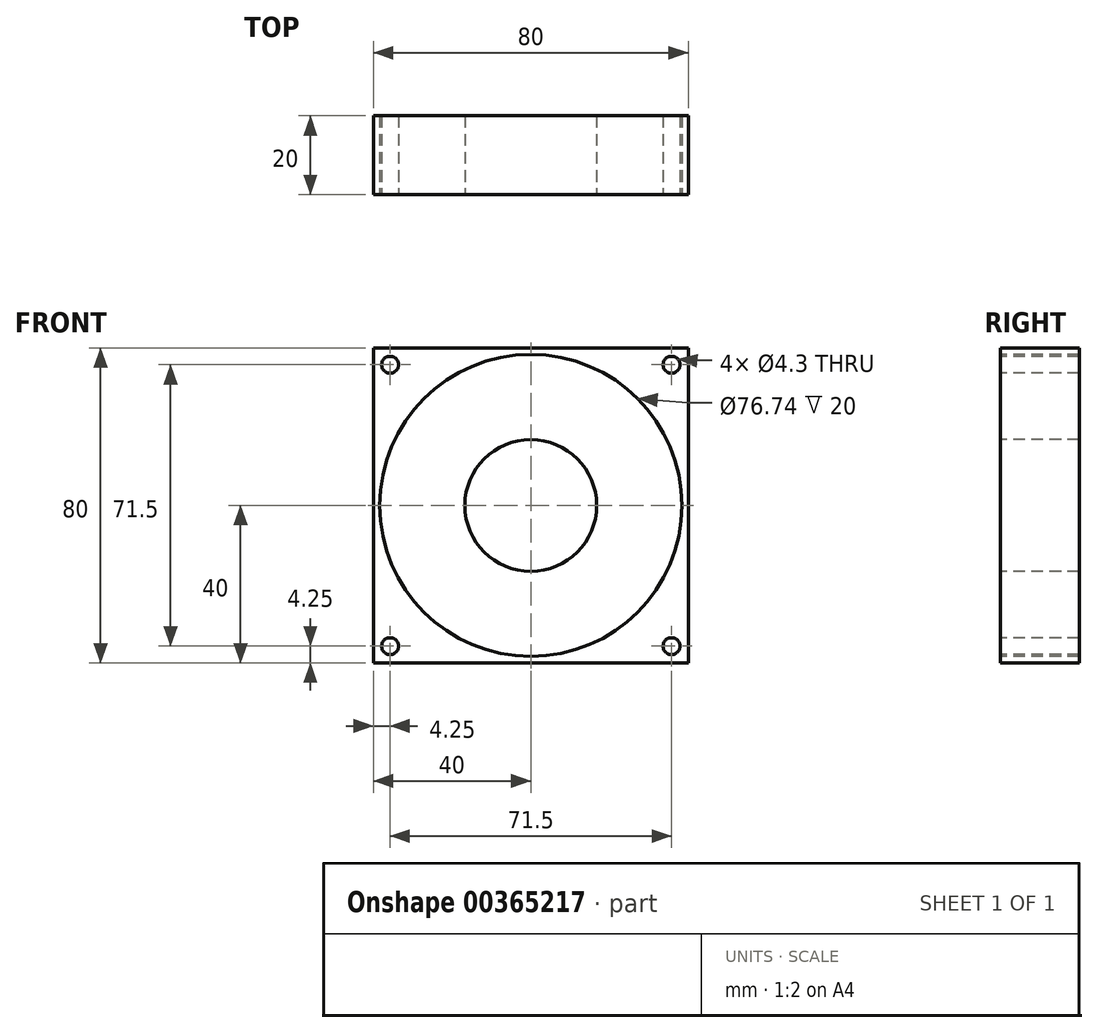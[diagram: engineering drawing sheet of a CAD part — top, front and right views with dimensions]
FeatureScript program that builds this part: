
annotation { "Feature Type Name" : "Feature", "Feature Type Description" : "" }
export const myFeature = defineFeature(function(context is Context, id is Id, definition is map)
    precondition{}
    {
        {
            var Q0;
            Q0=qCreatedBy(makeId("Front.planeOp"),FACE);
            var sketch = newSketch(context, id + "F0", { "sketchPlane" : qUnion([Q0])});
            skLineSegment(sketch, "E0.bottom", {"start": v(40, -40) * mm, "end": v(-40, -40) * mm});
            skLineSegment(sketch, "E0.top", {"start": v(40, 40) * mm, "end": v(-40, 40) * mm});
            skLineSegment(sketch, "E0.left", {"start": v(40, -40) * mm, "end": v(40, 40) * mm});
            skLineSegment(sketch, "E0.right", {"start": v(-40, -40) * mm, "end": v(-40, 40) * mm});
            skPoint(sketch, "E0.middle", {"position": v(0, 0) * mm});
            skSolve(sketch);
        }
        {
            var Q0;
            Q0 = qSketchRegion(id + "F0", true);
            extrude(context, id + "F1", {"entities" : qUnion([Q0]), "depth" : 20 * mm});
        }
        {
            var Q0;
            Q0=makeQuery(id+"F1.opExtrude","CAP_FACE",FACE,{"disambiguationData":[OSD([sQuery(id+"F0.wireOp",EDGE,"E0.bottom"),sQuery(id+"F0.wireOp",EDGE,"E0.top"),sQuery(id+"F0.wireOp",EDGE,"E0.left"),sQuery(id+"F0.wireOp",EDGE,"E0.right")])],"isStart":false});
            var sketch = newSketch(context, id + "F2", { "sketchPlane" : qUnion([Q0])});
            skLineSegment(sketch, "E1.bottom", {"start": v(35.75, -35.75) * mm, "end": v(-35.75, -35.75) * mm, "construction": true});
            skLineSegment(sketch, "E1.top", {"start": v(35.75, 35.75) * mm, "end": v(-35.75, 35.75) * mm, "construction": true});
            skLineSegment(sketch, "E1.left", {"start": v(35.75, -35.75) * mm, "end": v(35.75, 35.75) * mm, "construction": true});
            skLineSegment(sketch, "E1.right", {"start": v(-35.75, -35.75) * mm, "end": v(-35.75, 35.75) * mm, "construction": true});
            skPoint(sketch, "E1.middle", {"position": v(0, 0) * mm});
            skCircle(sketch, "E2", {"center": v(-35.75, 35.75) * mm, "radius": 2.15 * mm});
            skCircle(sketch, "E3.0.1.0", {"center": v(-35.75, -35.75) * mm, "radius": 2.15 * mm});
            skCircle(sketch, "E3.1.0.0", {"center": v(35.75, 35.75) * mm, "radius": 2.15 * mm});
            skCircle(sketch, "E3.1.1.0", {"center": v(35.75, -35.75) * mm, "radius": 2.15 * mm});
            skLineSegment(sketch, "E3.direction1", {"start": v(-35.75, 35.75) * mm, "end": v(35.75, 35.75) * mm, "construction": true});
            skLineSegment(sketch, "E3.direction2", {"start": v(-35.75, 35.75) * mm, "end": v(-35.75, -35.75) * mm, "construction": true});
            skSolve(sketch);
        }
        {
            var Q0;
            Q0 = qSketchRegion(id + "F2", true);
            extrude(context, id + "F3", {"entities" : qUnion([Q0]), "operationType" : NewBodyOperationType.REMOVE, "oppositeDirection" : true, "depth" : 25 * mm});
        }
        {
            var Q0;
            Q0=makeQuery(id+"F1.opExtrude","CAP_FACE",FACE,{"disambiguationData":[OSD([sQuery(id+"F0.wireOp",EDGE,"E0.bottom"),sQuery(id+"F0.wireOp",EDGE,"E0.top"),sQuery(id+"F0.wireOp",EDGE,"E0.left"),sQuery(id+"F0.wireOp",EDGE,"E0.right")])],"isStart":false});
            var sketch = newSketch(context, id + "F4", { "sketchPlane" : qUnion([Q0])});
            skCircle(sketch, "E4", {"center": v(0, 0) * mm, "radius": 16.74 * mm});
            skCircle(sketch, "E5", {"center": v(0, 0) * mm, "radius": 38.37 * mm});
            skSolve(sketch);
        }
        {
            var Q0;
            Q0=makeQuery(id+"F4.imprint","IMPRINT",FACE,{"disambiguationData":[TD([[makeQuery(id+"F4.imprint","IMPRINT",EDGE,{"derivedFrom":sQuery(id+"F4.wireOp",EDGE,"E4")}),-1.0]])]});
            extrude(context, id + "F5", {"entities" : qUnion([Q0]), "operationType" : NewBodyOperationType.REMOVE, "oppositeDirection" : true, "depth" : 25 * mm});
        }
    });
